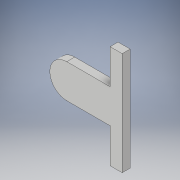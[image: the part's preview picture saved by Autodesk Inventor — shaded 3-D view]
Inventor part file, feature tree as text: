
AUTODESK INVENTOR PART (.ipt)
format: ipt  version: 2019 (Build 230136000, 136)  size: 103,936 bytes
history: native  units: in
note: dims shown in document units (in); Inventor stores cm internally (conversion verified against a paired STEP export)
features: extrude x1, sketch x1
ambient origin geometry x8: Origin, YZ Plane, XZ Plane, XY Plane, X Axis, Y Axis, Z Axis, Center Point
bodies: Solid1 (feature_tree)
feature tree (2):
  extrude  "Extrusion1"  Depth=0.7874in
  sketch  "Sketch1"  dims[d0=0.7677in d1=0.9843in d2=0.1811in d3=0.0in d4=0.7874in d5=0.2756in d6=0.7874in d7=2.3425in d8=0.7874in]
